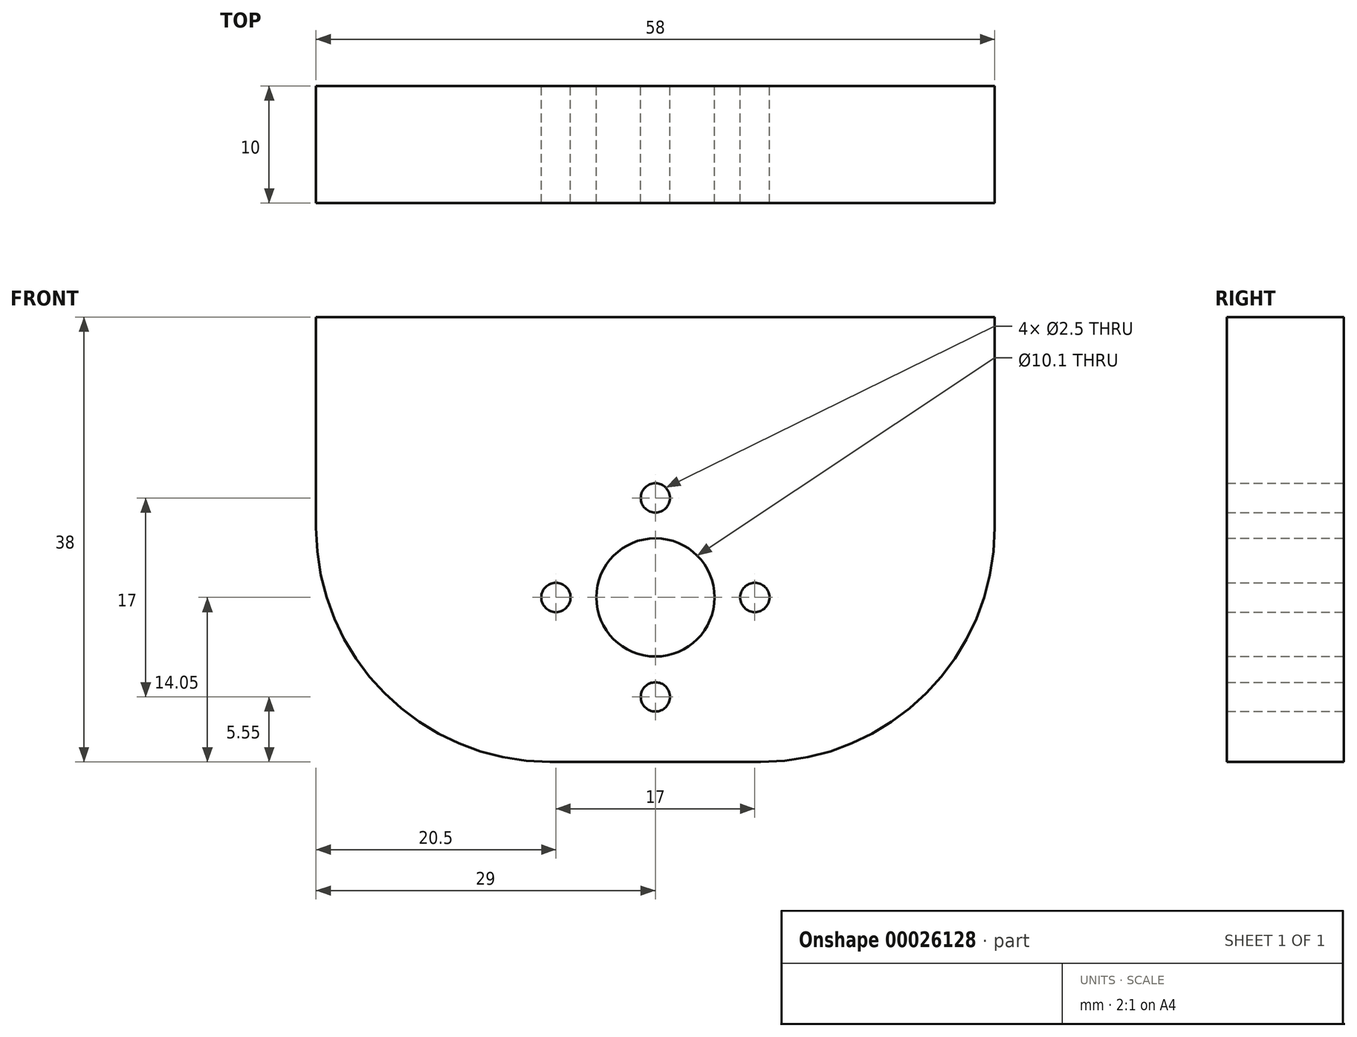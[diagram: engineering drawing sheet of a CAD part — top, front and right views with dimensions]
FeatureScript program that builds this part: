
annotation { "Feature Type Name" : "Feature", "Feature Type Description" : "" }
export const myFeature = defineFeature(function(context is Context, id is Id, definition is map)
    precondition{}
    {
        {
            var Q0;
            Q0=qCreatedBy(makeId("Front.planeOp"),FACE);
            var sketch = newSketch(context, id + "F0", { "sketchPlane" : qUnion([Q0])});
            skLineSegment(sketch, "E0.rect.bottom", {"start": v(-9, -19) * mm, "end": v(9, -19) * mm});
            skLineSegment(sketch, "E0.rect.top", {"start": v(-29, 19) * mm, "end": v(29, 19) * mm});
            skLineSegment(sketch, "E0.rect.left", {"start": v(-29, 1) * mm, "end": v(-29, 19) * mm});
            skLineSegment(sketch, "E0.rect.right", {"start": v(29, 1) * mm, "end": v(29, 19) * mm});
            skPoint(sketch, "E0.rect.middle", {"position": v(0, 0) * mm});
            skLineSegment(sketch, "E1", {"start": v(-29, 9) * mm, "end": v(29, 9) * mm, "construction": true});
            skCircle(sketch, "E2", {"center": v(0, -4.95) * mm, "radius": 5.05 * mm});
            skLineSegment(sketch, "E3", {"start": v(-8.5, -4.95) * mm, "end": v(8.5, -4.95) * mm, "construction": true});
            skCircle(sketch, "E4", {"center": v(-8.5, -4.95) * mm, "radius": 1.25 * mm});
            skCircle(sketch, "E5", {"center": v(8.5, -4.95) * mm, "radius": 1.25 * mm});
            skLineSegment(sketch, "E6", {"start": v(0, -13.45) * mm, "end": v(0, 3.55) * mm, "construction": true});
            skCircle(sketch, "E7", {"center": v(0, 3.55) * mm, "radius": 1.25 * mm});
            skCircle(sketch, "E8", {"center": v(0, -13.45) * mm, "radius": 1.25 * mm});
            skPoint(sketch, "E9", {"position": v(0, -10) * mm});
            skLineSegment(sketch, "E10", {"start": v(-29, -10) * mm, "end": v(29, -10) * mm, "construction": true});
            skPoint(sketch, "E11.visualSharp", {"position": v(29, -19) * mm});
            skArc(sketch, "E11.filletArc", {"start": v(9, -19) * mm, "mid": v(23.14, -13.14) * mm, "end": v(29, 1) * mm});
            skPoint(sketch, "E12.visualSharp", {"position": v(-29, -19) * mm});
            skArc(sketch, "E12.filletArc", {"start": v(-29, 1) * mm, "mid": v(-23.14, -13.14) * mm, "end": v(-9, -19) * mm});
            skSolve(sketch);
        }
        {
            var Q0;
            Q0=makeQuery(id+"F0.imprint","IMPRINT",FACE,{"disambiguationData":[TD([[makeQuery(id+"F0.imprint","IMPRINT",EDGE,{"derivedFrom":sQuery(id+"F0.wireOp",EDGE,"E0.rect.bottom")}),1.0]])]});
            extrude(context, id + "F1", {"entities" : qUnion([Q0]), "endBound" : BoundingType.SYMMETRIC, "depth" : 10 * mm});
        }
    });
